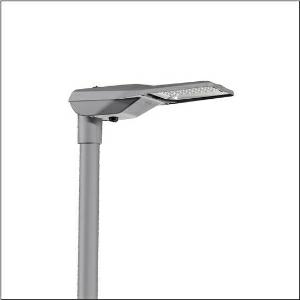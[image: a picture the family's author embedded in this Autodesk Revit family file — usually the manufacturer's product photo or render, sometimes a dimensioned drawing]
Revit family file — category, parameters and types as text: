
# Revit family: streetlight_sl_21_mini___p1_0a_5xe2a43t08gb_2ff8
name_source: partatom
category: Lighting Fixtures
units: mm (PartAtom-declared; Revit-internal decimal feet)

## family parameters
Cut with Voids When Loaded = No
Host = Face
Light Source = No
Part Type = Normal
Room Calculation Point = No
Round Connector Dimension = Use Diameter
Shared = No

## types (1)
- --- (1 x LED, 6180 lm, 40.4 W, 4000K)
    Apparent Load = 40 VA
    CIE Flux Codes = 21 50 90 100 100
    Color Rendering = 70
    Color Temperature = 4000K
    Default Elevation = 1800 mm
    Description = Streetlight SL 21 mini, mast luminaire, primary light control with lens, of PMMA, primary optical cover: cover, of toughened safety glass, transparent, light distribution: P1.0a, light emission: direct distribution, primary light characteristic: asymmetric, installation type: side-entry, post-top, LED, High Power LED, rated luminous flux: 6.180lm, luminous efficacy: 153lm/W, light colour: 740, colour temperature: 4000K, control gear: D4i, control: overheat protection, constant luminous flux control, time-dependent luminous flux control, flexible luminous flux parameterisation, pre-setting: logarithmic dimming characteristic, mains connection: 220..240V, AC, 50/60Hz, start of lifetime: 40W, end of service life: 41W, reduction: 19W, luminaire housing, of diecast aluminium, powder-coated, Siteco® metallic grey (DB 702S), corrosivity category C5 mid according to DIN EN ISO 12944, please order mast flange separately, inclination adjustable: 0°, 5°, 10°, 15°, sealing non-destructively replaceable, multi-level sealing system, length: 628mm, width: 235mm, height: 110mm, mast flange for spigot size: 42mm (side-entry): 5XC10008XM4, 60/48mm (side-entry/post-top): 5XC10108XM2, 76/60mm (side-entry/post-top): 5XC10108XM1, mounting height: 4..8m, Smart Interface below and above, protection rating (complete): IP66, insulation class (complete): insulation class II (safety insulation), certification: CE, ENEC, ENEC+, VDE, impact resistance: IK10, permissible operating ambient temperature for outdoor applications: -40..+50°C, standard-compliant lighting for roads and squares, packaging unit: 1 piece

Light Distribution: P1.0a
    Height = 110 mm
    Lamp = 1 x LED
    Lamp Light Flux = 6180 lm
    Lamp Power = 40.4 W
    Lamp count = 1
    Length = 625 mm
    Luminous efficacy = 153 lm/W
    Manufacturer = Siteco
    ModVariant = No
    Model = 5XE2A43T08GB
    Number of Poles = 1
    OnlyDefault = Yes
    Power Factor = 1
    Product Name = Streetlight SL 21 mini | P1.0a
    Product group = mast luminaire | pylon top
    ProductGroupID = 6100
    Protection Class = Protection class II
    Protection Degree = IP 66
    RLX_Detail_Level = 1
    RLX_Emergency_Light_Flux = 0 lm
    RLX_Emergency_Type = 0
    RLX_Emergency_Type_DB = No
    RlxData = <blob elided: 37553 chars, md5=3507e409>
    Socket = socket
    Standby Power = 0 W
    System Light Flux = 6180 lm
    System Power = 40 W
    Type Comments = factory setting: luminous flux: 100 % | dim-lin: 254 | 812 mA
    Type Image = l_1003514.jpg
    URL = http://relux.com
    VarID = @adj_186514
    Voltage = 0 V
    Weight = 0.00 kg
    Width = 234 mm

## geometry (parser evidence)
native form markers: Blend x4, Sweep x9
no freeform markers — native parametric forms only
